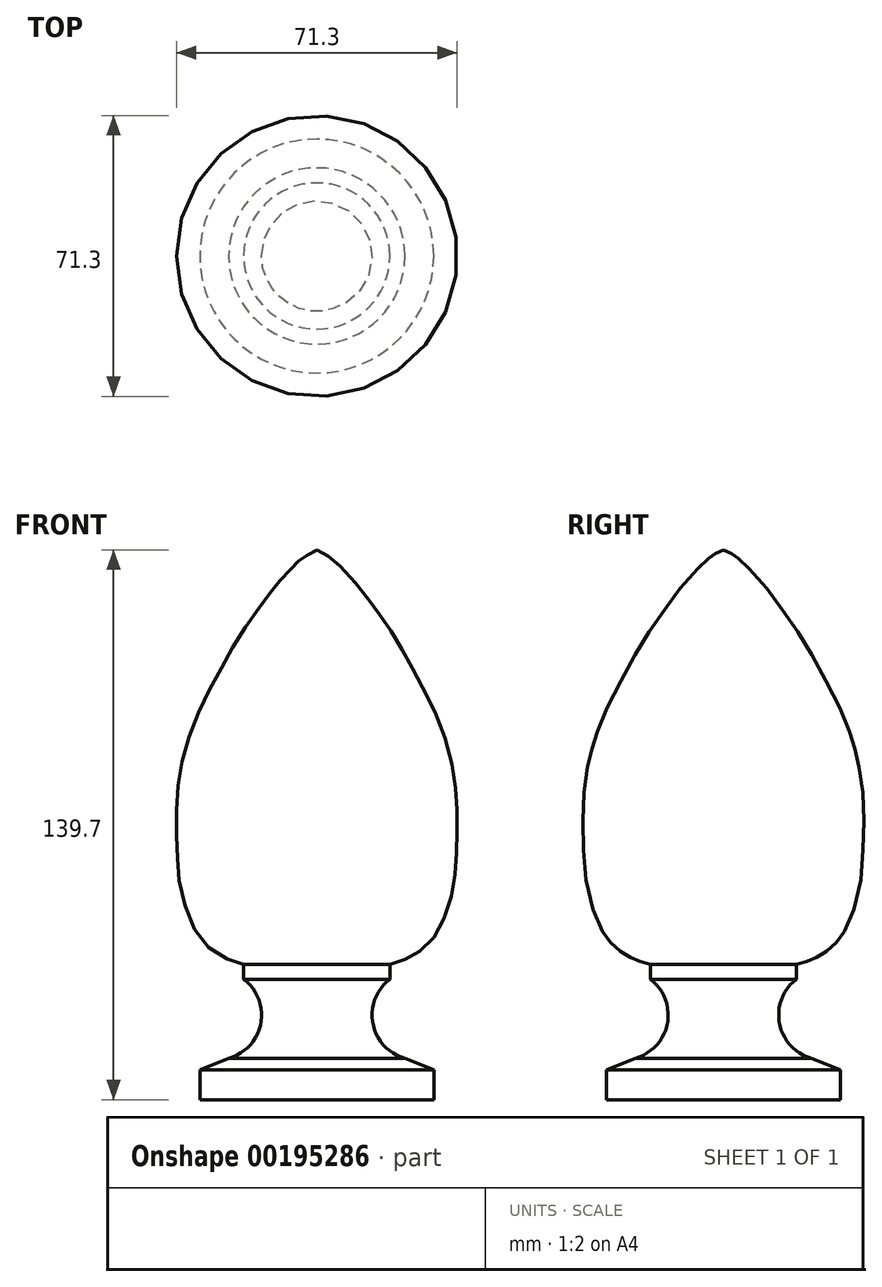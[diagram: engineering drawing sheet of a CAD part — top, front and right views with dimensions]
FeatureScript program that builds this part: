
annotation { "Feature Type Name" : "Feature", "Feature Type Description" : "" }
export const myFeature = defineFeature(function(context is Context, id is Id, definition is map)
    precondition{}
    {
        {
            var Q0;
            Q0=qCreatedBy(makeId("Front.planeOp"),FACE);
            var sketch = newSketch(context, id + "F0", { "sketchPlane" : qUnion([Q0])});
            skLineSegment(sketch, "E0", {"start": v(0, 0) * mm, "end": v(0, 139.7) * mm});
            skLineSegment(sketch, "E1", {"start": v(0, 0) * mm, "end": v(-29.72, 0) * mm});
            skLineSegment(sketch, "E2", {"start": v(-29.72, 0) * mm, "end": v(-29.72, 7.62) * mm});
            skLineSegment(sketch, "E3", {"start": v(-29.72, 7.62) * mm, "end": v(-20.1, 11.43) * mm});
            skLineSegment(sketch, "E4", {"start": v(-18.58, 34.4) * mm, "end": v(-18.58, 34.4) * mm});
            skLineSegment(sketch, "E5", {"start": v(-18.58, 34.4) * mm, "end": v(-18.58, 30.58) * mm});
            skArc(sketch, "E6", {"start": v(-22.39, 10.52) * mm, "mid": v(-14.23, 19.37) * mm, "end": v(-18.58, 30.58) * mm});
            skFitSpline(sketch, "E7", {"points": [v(0, 139.7) * mm, v(-2.09, 138.63) * mm, v(-3.65, 137.58) * mm, v(-5.4, 136.1) * mm, v(-7.32, 133.98) * mm, v(-10.59, 130.47) * mm, v(-13.7, 126.27) * mm, v(-19.43, 118.11) * mm, v(-24.6, 109) * mm, v(-30.01, 98.51) * mm, v(-33.98, 86.84) * mm, v(-35.56, 75.6) * mm, v(-35.52, 64.14) * mm, v(-34.86, 55.11) * mm, v(-30.96, 43.13) * mm, v(-24.65, 36.7) * mm, v(-18.58, 34.4) * mm], "startDerivative": vector(-111.78, -42.92) * mm, "endDerivative": vector(61.66, -7.74) * mm});
            skLineSegment(sketch, "E8", {"start": v(0, 139.7) * mm, "end": v(-95.76, 139.7) * mm, "construction": true});
            skSolve(sketch);
        }
        {
            var Q0;
            Q0=makeQuery(id+"F0.imprint","IMPRINT",FACE,{"disambiguationData":[TD([[makeQuery(id+"F0.imprint","IMPRINT",EDGE,{"derivedFrom":sQuery(id+"F0.wireOp",EDGE,"E0")}),1.0]])]});
            var Q1;
            Q1=sQuery(id+"F0.wireOp",EDGE,"E7");
            var Q2;
            Q2=sQuery(id+"F0.wireOp",EDGE,"E5");
            var Q3;
            Q3=sQuery(id+"F0.wireOp",EDGE,"E6");
            var Q4;
            Q4=sQuery(id+"F0.wireOp",EDGE,"E3");
            var Q5;
            Q5=sQuery(id+"F0.wireOp",EDGE,"E2");
            var Q6;
            Q6=sQuery(id+"F0.wireOp",EDGE,"E1");
            var Q7;
            Q7=sQuery(id+"F0.wireOp",EDGE,"E0");
            revolve(context, id + "F1", {"entities" : qUnion([Q0]), "surfaceEntities" : qUnion([Q1, Q2, Q3, Q4, Q5, Q6]), "axis" : qUnion([Q7]), "revolveType" : RevolveType.FULL});
        }
    });
